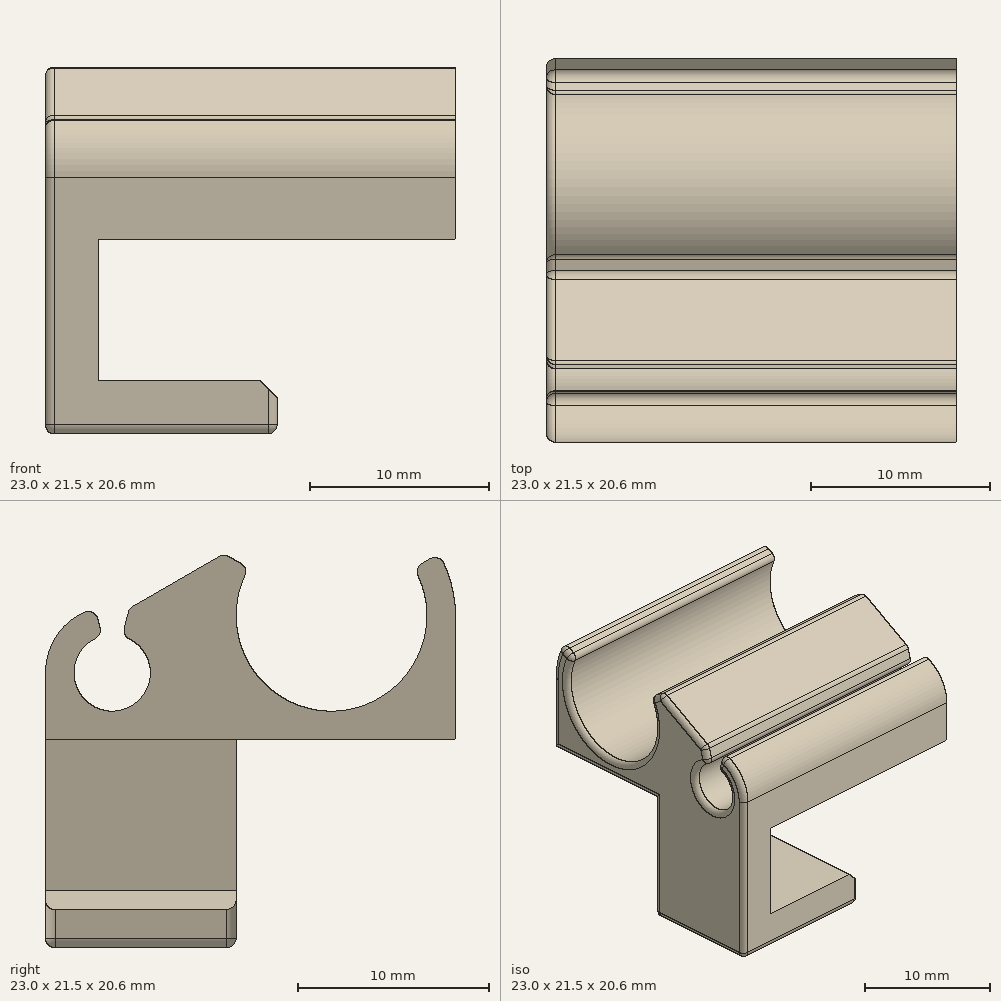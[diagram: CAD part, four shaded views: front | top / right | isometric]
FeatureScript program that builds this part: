
annotation { "Feature Type Name" : "Feature", "Feature Type Description" : "" }
export const myFeature = defineFeature(function(context is Context, id is Id, definition is map)
    precondition{}
    {
        {
            var Q0;
            Q0=qCreatedBy(makeId("Right.planeOp"),FACE);
            var sketch = newSketch(context, id + "F0", { "sketchPlane" : qUnion([Q0])});
            skLineSegment(sketch, "E0", {"start": v(0, 0) * mm, "end": v(-21.5, 0) * mm});
            skLineSegment(sketch, "E1", {"start": v(-6.5, 6.5) * mm, "end": v(-6.5, 0) * mm, "construction": true});
            skLineSegment(sketch, "E2", {"start": v(-18, 3.5) * mm, "end": v(-18, 0) * mm, "construction": true});
            skLineSegment(sketch, "E3", {"start": v(-18, 3.5) * mm, "end": v(-16.55, 8.9) * mm, "construction": true});
            skLineSegment(sketch, "E4", {"start": v(-18, 3.5) * mm, "end": v(-19.43, 8.82) * mm, "construction": true});
            skLineSegment(sketch, "E5", {"start": v(-6.5, 6.5) * mm, "end": v(1.8, 11.3) * mm, "construction": true});
            skLineSegment(sketch, "E6", {"start": v(-6.5, 6.5) * mm, "end": v(-15.63, 11.77) * mm, "construction": true});
            skArc(sketch, "E7", {"start": v(-10.83, 9) * mm, "mid": v(-6.5, 1.5) * mm, "end": v(-2.17, 9) * mm});
            skArc(sketch, "E8", {"start": v(-2.17, 9) * mm, "mid": v(-6.5, 11.5) * mm, "end": v(-10.83, 9) * mm, "construction": true});
            skArc(sketch, "E9", {"start": v(-0.87, 9.75) * mm, "mid": v(-6.5, 13) * mm, "end": v(-12.13, 9.75) * mm, "construction": true});
            skArc(sketch, "E10", {"start": v(-12.13, 9.75) * mm, "mid": v(-8.18, 0.22) * mm, "end": v(0, 6.5) * mm, "construction": true});
            skArc(sketch, "E11", {"start": v(-17.1, 6.88) * mm, "mid": v(-18, 7) * mm, "end": v(-18.9, 6.88) * mm, "construction": true});
            skArc(sketch, "E12", {"start": v(-18.9, 6.88) * mm, "mid": v(-20.78, 5.63) * mm, "end": v(-21.5, 3.5) * mm});
            skArc(sketch, "E13", {"start": v(-18.52, 5.43) * mm, "mid": v(-18, 1.5) * mm, "end": v(-17.48, 5.43) * mm});
            skArc(sketch, "E14", {"start": v(-17.48, 5.43) * mm, "mid": v(-18, 5.5) * mm, "end": v(-18.52, 5.43) * mm, "construction": true});
            skLineSegment(sketch, "E15", {"start": v(-17.48, 5.43) * mm, "end": v(-17.1, 6.88) * mm});
            skLineSegment(sketch, "E16", {"start": v(-18.52, 5.43) * mm, "end": v(-18.9, 6.88) * mm});
            skLineSegment(sketch, "E17", {"start": v(-10.83, 9) * mm, "end": v(-12.13, 9.75) * mm});
            skLineSegment(sketch, "E18", {"start": v(-2.17, 9) * mm, "end": v(-0.87, 9.75) * mm});
            skLineSegment(sketch, "E19", {"start": v(-17.1, 6.88) * mm, "end": v(-12.13, 9.75) * mm});
            skLineSegment(sketch, "E20", {"start": v(-21.5, 0) * mm, "end": v(-21.5, 3.5) * mm});
            skLineSegment(sketch, "E21", {"start": v(0, 0) * mm, "end": v(0, 6.5) * mm});
            skArc(sketch, "E22", {"start": v(0, 6.5) * mm, "mid": v(-0.22, 8.18) * mm, "end": v(-0.87, 9.75) * mm});
            skArc(sketch, "E23", {"start": v(-21.5, 3.5) * mm, "mid": v(-15.87, 0.72) * mm, "end": v(-17.1, 6.88) * mm, "construction": true});
            skSolve(sketch);
        }
        {
            var Q0;
            Q0=makeQuery(id+"F0.imprint","IMPRINT",FACE,{"disambiguationData":[TD([[makeQuery(id+"F0.imprint","IMPRINT",EDGE,{"derivedFrom":sQuery(id+"F0.wireOp",EDGE,"E0")}),-1.0]])]});
            extrude(context, id + "F1", {"entities" : qUnion([Q0]), "depth" : 23 * mm});
        }
        {
            var Q0;
            Q0=makeQuery(id+"F1.opExtrude","SWEPT_FACE",FACE,{"disambiguationData":[OSD([sQuery(id+"F0.wireOp",EDGE,"E20")])]});
            var sketch = newSketch(context, id + "F2", { "sketchPlane" : qUnion([Q0])});
            skLineSegment(sketch, "E24", {"start": v(0, 0) * mm, "end": v(0, -10.9) * mm});
            skLineSegment(sketch, "E25", {"start": v(0, -10.9) * mm, "end": v(13, -10.9) * mm});
            skLineSegment(sketch, "E26", {"start": v(13, -10.9) * mm, "end": v(13, -7.9) * mm});
            skLineSegment(sketch, "E27", {"start": v(13, -7.9) * mm, "end": v(3, -7.9) * mm});
            skLineSegment(sketch, "E28", {"start": v(3, -7.9) * mm, "end": v(3, 0) * mm});
            skLineSegment(sketch, "E29", {"start": v(3, 0) * mm, "end": v(0, 0) * mm});
            skSolve(sketch);
        }
        {
            var Q0;
            Q0=makeQuery(id+"F2.imprint","IMPRINT",FACE,{"disambiguationData":[TD([[makeQuery(id+"F2.imprint","IMPRINT",EDGE,{"derivedFrom":sQuery(id+"F2.wireOp",EDGE,"E24")}),1.0]])]});
            extrude(context, id + "F3", {"entities" : qUnion([Q0]), "operationType" : NewBodyOperationType.ADD, "oppositeDirection" : true, "depth" : 10 * mm});
        }
        {
            var Q0;
            Q0=makeQuery(id+"F1.opExtrude","CAP_EDGE",EDGE,{"disambiguationData":[OSD([sQuery(id+"F0.wireOp",EDGE,"E13")])],"isStart":true});
            var Q1;
            Q1=makeQuery(id+"F1.opExtrude","CAP_EDGE",EDGE,{"disambiguationData":[OSD([sQuery(id+"F0.wireOp",EDGE,"E15")])],"isStart":true});
            var Q2;
            Q2=makeQuery(id+"F1.opExtrude","CAP_EDGE",EDGE,{"disambiguationData":[OSD([sQuery(id+"F0.wireOp",EDGE,"E19")])],"isStart":true});
            var Q3;
            Q3=makeQuery(id+"F1.opExtrude","CAP_EDGE",EDGE,{"disambiguationData":[OSD([sQuery(id+"F0.wireOp",EDGE,"E17")])],"isStart":true});
            var Q4;
            Q4=makeQuery(id+"F1.opExtrude","CAP_EDGE",EDGE,{"disambiguationData":[OSD([sQuery(id+"F0.wireOp",EDGE,"E7")])],"isStart":true});
            var Q5;
            Q5=makeQuery(id+"F1.opExtrude","CAP_EDGE",EDGE,{"disambiguationData":[OSD([sQuery(id+"F0.wireOp",EDGE,"E18")])],"isStart":true});
            var Q6;
            Q6=makeQuery(id+"F1.opExtrude","CAP_EDGE",EDGE,{"disambiguationData":[OSD([sQuery(id+"F0.wireOp",EDGE,"E21")])],"isStart":true});
            var Q7;
            Q7=makeQuery(id+"F1.opExtrude","CAP_EDGE",EDGE,{"disambiguationData":[OSD([sQuery(id+"F0.wireOp",EDGE,"E0")])],"isStart":true});
            var Q8;
            Q8=makeQuery(id+"F3.opExtrude","CAP_EDGE",EDGE,{"disambiguationData":[OSD([sQuery(id+"F2.wireOp",EDGE,"E24")])],"isStart":false});
            var Q9;
            Q9=makeQuery(id+"F3.opExtrude","SWEPT_EDGE",EDGE,{"disambiguationData":[OSD([sQuery(id+"F2.wireOp",EDGE,"E24"),sQuery(id+"F2.wireOp",EDGE,"E25")])]});
            var Q10;
            Q10=makeQuery(id+"F3.boolean.opBoolean","MERGE",EDGE,{"derivedFrom":[makeQuery(id+"F1.opExtrude","CAP_EDGE",EDGE,{"disambiguationData":[OSD([sQuery(id+"F0.wireOp",EDGE,"E20")])],"isStart":true}),makeQuery(id+"F3.opExtrude","CAP_EDGE",EDGE,{"disambiguationData":[OSD([sQuery(id+"F2.wireOp",EDGE,"E24")])],"isStart":true})]});
            var Q11;
            Q11=makeQuery(id+"F1.opExtrude","CAP_EDGE",EDGE,{"disambiguationData":[OSD([sQuery(id+"F0.wireOp",EDGE,"E16")])],"isStart":true});
            var Q12;
            Q12=makeQuery(id+"F3.opExtrude","CAP_EDGE",EDGE,{"disambiguationData":[OSD([sQuery(id+"F2.wireOp",EDGE,"E25")])],"isStart":true});
            var Q13;
            Q13=makeQuery(id+"F3.opExtrude","CAP_EDGE",EDGE,{"disambiguationData":[OSD([sQuery(id+"F2.wireOp",EDGE,"E25")])],"isStart":false});
            var Q14;
            Q14=makeQuery(id+"F3.opExtrude","SWEPT_EDGE",EDGE,{"disambiguationData":[OSD([sQuery(id+"F2.wireOp",EDGE,"E25"),sQuery(id+"F2.wireOp",EDGE,"E26")])]});
            var Q15;
            Q15=makeQuery(id+"F3.opExtrude","CAP_EDGE",EDGE,{"disambiguationData":[OSD([sQuery(id+"F2.wireOp",EDGE,"E26")])],"isStart":false});
            var Q16;
            Q16=makeQuery(id+"F3.opExtrude","CAP_EDGE",EDGE,{"disambiguationData":[OSD([sQuery(id+"F2.wireOp",EDGE,"E26")])],"isStart":true});
            var Q17;
            Q17=makeQuery(id+"F1.opExtrude","SWEPT_EDGE",EDGE,{"disambiguationData":[OSD([sQuery(id+"F0.wireOp",EDGE,"E13"),sQuery(id+"F0.wireOp",EDGE,"E15")])]});
            var Q18;
            Q18=makeQuery(id+"F1.opExtrude","SWEPT_EDGE",EDGE,{"disambiguationData":[OSD([sQuery(id+"F0.wireOp",EDGE,"E15"),sQuery(id+"F0.wireOp",EDGE,"E19")])]});
            var Q19;
            Q19=makeQuery(id+"F1.opExtrude","SWEPT_EDGE",EDGE,{"disambiguationData":[OSD([sQuery(id+"F0.wireOp",EDGE,"E13"),sQuery(id+"F0.wireOp",EDGE,"E16")])]});
            var Q20;
            Q20=makeQuery(id+"F1.opExtrude","SWEPT_EDGE",EDGE,{"disambiguationData":[OSD([sQuery(id+"F0.wireOp",EDGE,"E12"),sQuery(id+"F0.wireOp",EDGE,"E16")])]});
            var Q21;
            Q21=makeQuery(id+"F1.opExtrude","SWEPT_EDGE",EDGE,{"disambiguationData":[OSD([sQuery(id+"F0.wireOp",EDGE,"E17"),sQuery(id+"F0.wireOp",EDGE,"E19")])]});
            var Q22;
            Q22=makeQuery(id+"F1.opExtrude","SWEPT_EDGE",EDGE,{"disambiguationData":[OSD([sQuery(id+"F0.wireOp",EDGE,"E7"),sQuery(id+"F0.wireOp",EDGE,"E17")])]});
            var Q23;
            Q23=makeQuery(id+"F1.opExtrude","SWEPT_EDGE",EDGE,{"disambiguationData":[OSD([sQuery(id+"F0.wireOp",EDGE,"E7"),sQuery(id+"F0.wireOp",EDGE,"E18")])]});
            var Q24;
            Q24=makeQuery(id+"F1.opExtrude","SWEPT_EDGE",EDGE,{"disambiguationData":[OSD([sQuery(id+"F0.wireOp",EDGE,"E18"),sQuery(id+"F0.wireOp",EDGE,"E22")])]});
            fillet(context, id + "F4", {"entities" : qUnion([Q0, Q1, Q2, Q3, Q4, Q5, Q6, Q7, Q8, Q9, Q10, Q11, Q12, Q13, Q14, Q15, Q16, Q17, Q18, Q19, Q20, Q21, Q22, Q23, Q24]), "radius" : 0.5 * mm, "tangentPropagation" : true, "allowEdgeOverflow" : false});
        }
        {
            var Q0;
            Q0=makeQuery(id+"F3.opExtrude","SWEPT_EDGE",EDGE,{"disambiguationData":[OSD([sQuery(id+"F2.wireOp",EDGE,"E26"),sQuery(id+"F2.wireOp",EDGE,"E27")])]});
            chamfer(context, id + "F5", {"entities" : qUnion([Q0]), "width" : 1 * mm});
        }
    });
